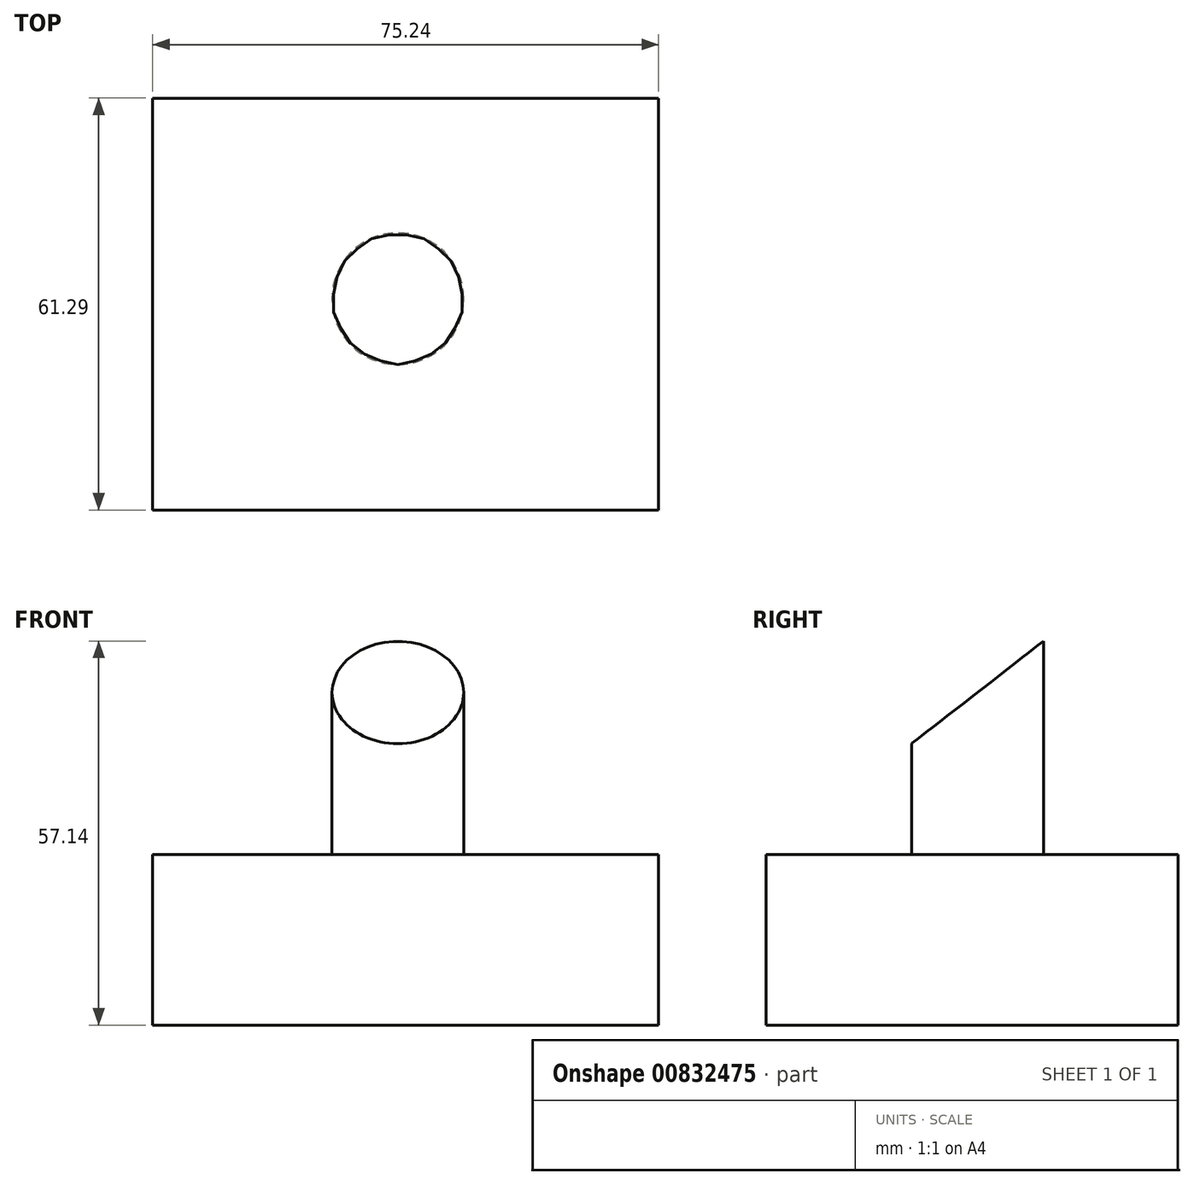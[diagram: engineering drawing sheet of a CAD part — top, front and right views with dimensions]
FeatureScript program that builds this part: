
annotation { "Feature Type Name" : "Feature", "Feature Type Description" : "" }
export const myFeature = defineFeature(function(context is Context, id is Id, definition is map)
    precondition{}
    {
        {
            var Q0;
            Q0=qCreatedBy(makeId("Top.planeOp"),FACE);
            var sketch = newSketch(context, id + "F0", { "sketchPlane" : qUnion([Q0])});
            skLineSegment(sketch, "E0.bottom", {"start": v(38.77, -18.81) * mm, "end": v(-36.47, -18.81) * mm});
            skLineSegment(sketch, "E0.top", {"start": v(38.77, 42.48) * mm, "end": v(-36.47, 42.48) * mm});
            skLineSegment(sketch, "E0.left", {"start": v(38.77, -18.81) * mm, "end": v(38.77, 42.48) * mm});
            skLineSegment(sketch, "E0.right", {"start": v(-36.47, -18.81) * mm, "end": v(-36.47, 42.48) * mm});
            skCircle(sketch, "E1", {"center": v(0, 12.63) * mm, "radius": 9.8 * mm});
            skSolve(sketch);
        }
        {
            var Q0;
            Q0 = qSketchRegion(id + "F0", true);
            extrude(context, id + "F1", {"entities" : qUnion([Q0]), "depth" : 25.4 * mm, "offsetDistance" : 25.4 * mm});
        }
        {
            var Q0;
            Q0=makeQuery(id+"F0.imprint","IMPRINT",FACE,{"disambiguationData":[TD([[makeQuery(id+"F0.imprint","IMPRINT",EDGE,{"derivedFrom":sQuery(id+"F0.wireOp",EDGE,"E1")}),1.0]])]});
            extrude(context, id + "F2", {"entities" : qUnion([Q0]), "operationType" : NewBodyOperationType.ADD, "depth" : 57.15 * mm, "offsetDistance" : 25.4 * mm});
        }
        {
            var Q0;
            Q0=qCreatedBy(makeId("Right.planeOp"),FACE);
            var sketch = newSketch(context, id + "F3", { "sketchPlane" : qUnion([Q0])});
            skLineSegment(sketch, "E2", {"start": v(-4.33, 36.3) * mm, "end": v(35.59, 67.38) * mm});
            skLineSegment(sketch, "E3", {"start": v(35.59, 67.38) * mm, "end": v(-5.74, 67.38) * mm});
            skLineSegment(sketch, "E4", {"start": v(-5.74, 67.38) * mm, "end": v(-4.33, 36.3) * mm});
            skSolve(sketch);
        }
        {
            var Q0;
            Q0 = qSketchRegion(id + "F3", true);
            extrude(context, id + "F4", {"entities" : qUnion([Q0]), "operationType" : NewBodyOperationType.REMOVE, "endBound" : BoundingType.SYMMETRIC, "oppositeDirection" : true, "depth" : 47.75 * mm, "offsetDistance" : 25.4 * mm});
        }
    });
